# Revit family: Electronics_Visual-Projectors_ViewSonic_The-ViewSonicR-PRO8800WUL-Projector
name_source: partatom
category: Electrical Equipment
revit_build: Autodesk Revit 2015 (Build: 20140606_1530(x64)
units: mm (PartAtom-declared; Revit-internal decimal feet)

## types (1)
- 8800WUL
    Assembly Code = D50
    BIMobject category = Visual - Projectors
    BIMobject category code = electronics-visual-projectors
    BIMobject main category = Electronics
    BIMobject main category code = electronics
    BOSUseNativeGeometries = 1
    Brand url = https://www.viewsonic.com
    Covering Color = Plastic - Viewsonic - White
    Description = Delivering stunning WUXGA 1920x1200 resolution and 5200 lumens of brightness, the ViewSonic® LightStream® Pro8800WUL is the ideal projector for professional installations, large venues, and business and education environments. With its 1.6x optical zoom, centered lens, vertical lens shift, and HV keystoning, the Pro8800WUL provides extreme flexibility even in the most challenging installations. Pro8800WUL includes a sleek top cover design for quick lamp and accessory access, while an intuitive PortAll® compartment accommodates additional accessories such as an HDBT receiver, wireless streaming device, or PC stick. The cable management hood hides unsightly cables, and a 4-in-1 power button serves as a central point for LED notifications. Moreover, four HDMI ports and additional audio and video ports allow for extensive connectivity to handle multiple devices without the need to switch cables. Powered by SuperColor™ technology for amazing images, and SonicExpert® technology for incredibly clear sound, the Pro8800HDL delivers professional audiovisual performance.
    Design country = Taiwan
    Edition number = 1
    Keynote = V90
    Manufacturer = ViewSonic
    Manufacturer country = Taiwan
    Manufacturer name = ViewSonic
    Model = viewsonic_8800wul
    Product Guid = 58537fe3-2c9a-42dd-bce0-00ac5c4b8deb
    Product SKU = viewsonic_8800WUL
    Product data url = https://bimobject.com
    Product family = Electronics
    Product group = Projectors
    Product name = The ViewSonic® 8800UL Projector
    Product url = https://www.viewsonic.com
    QR code = http://bimobject.com
    URL = www.viewsonic.com
    a = Image Aspect Ratio : "4  - 3"
    b = Image Aspect Ratio : "16 - 9"
    c = Image Aspect Ratio : "16 - 10"

## geometry (parser evidence)
native form markers: Blend x2, Sweep x7
no freeform markers — native parametric forms only
